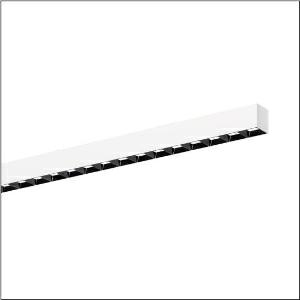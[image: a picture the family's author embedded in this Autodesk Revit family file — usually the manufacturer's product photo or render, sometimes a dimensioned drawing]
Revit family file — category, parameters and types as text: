
# Revit family: silica_r__21_51mx24dc3awb_4576
name_source: partatom
category: Lighting Fixtures
units: mm (PartAtom-declared; Revit-internal decimal feet)

## family parameters
Cut with Voids When Loaded = No
Host = Face
Light Source = No
Part Type = Normal
Room Calculation Point = No
Round Connector Dimension = Use Diameter
Shared = No

## types (1)
- --- (1 x LED, 10800 lm, 79 W, 3000K)
    Apparent Load = 79 VA
    CIE Flux Codes = 74 94 99 100 100
    Color Rendering = 80
    Color Temperature = 3000K
    Default Elevation = 1800 mm
    Description = Silica® 21, office luminaire, primary light control with darklight reflector, of PMMA, black, CAT 2 (L<= 3000cd/m²), light emission: direct distribution, primary light characteristic: asymmetric, installation type: surface-mounted, LED, rated luminous flux: 10.800lm, luminous efficacy: 137lm/W, light colour: 830, colour temperature: 3000K, with terminal, 3+2-pole, max. 2.5mm², mains connection: 220..240V, AC, 50/60Hz, rated input power: 79W, luminaire housing, of aluminium, traffic white (RAL 9016), length: 3.004mm, width: 53mm, height: 53mm, protection rating (complete): IP20, insulation class (complete): insulation class I (protective earthing), certification: CE, permissible operating ambient temperature: 0..+35°C, standard: EN 50419, packaging unit: 1 piece
    Height = 0 mm  [stored 0 ft]
    Lamp = 1 x LED
    Lamp Light Flux = 10800 lm
    Lamp Power = 79 W
    Lamp count = 1
    Length = 3004 mm
    Luminous efficacy = 137 lm/W
    Manufacturer = Siteco
    ModVariant = No
    Model = 51MX24DC3AWB
    Mounting Place = Ceiling
    Mounting Type = Recessed
    Number of Poles = 1
    OnlyDefault = Yes
    Power Factor = 1
    Product Name = Silica® 21
    Product group = office luminaire | ceiling recessed
    ProductGroupID = 400
    Protection Class = Protection class I
    Protection Degree = IP 20
    RLX_Detail_Level = 1
    RLX_Emergency_Light_Flux = 0 lm
    RLX_Emergency_Type = 0
    RLX_Emergency_Type_DB = No
    RlxData = <blob elided: 62497 chars, md5=0407284a>
    Socket = socket
    Standby Power = 0 W
    System Light Flux = 10800 lm
    System Power = 79 W
    Type Comments = factory setting: luminous flux: 100 % | dim-lin: 254 | 448 mA
    Type Image = l_1335873.jpg
    URL = http://relux.com
    VarID = @adj_092579
    Voltage = 0 V
    Weight = 0.00 kg
    Width = 53 mm

note: [stored X ft] marks values corroborated as IEEE doubles in the binary element streams (Revit-internal decimal feet)

## geometry (parser evidence)
native form markers: Blend x4, Sweep x10
no freeform markers — native parametric forms only
